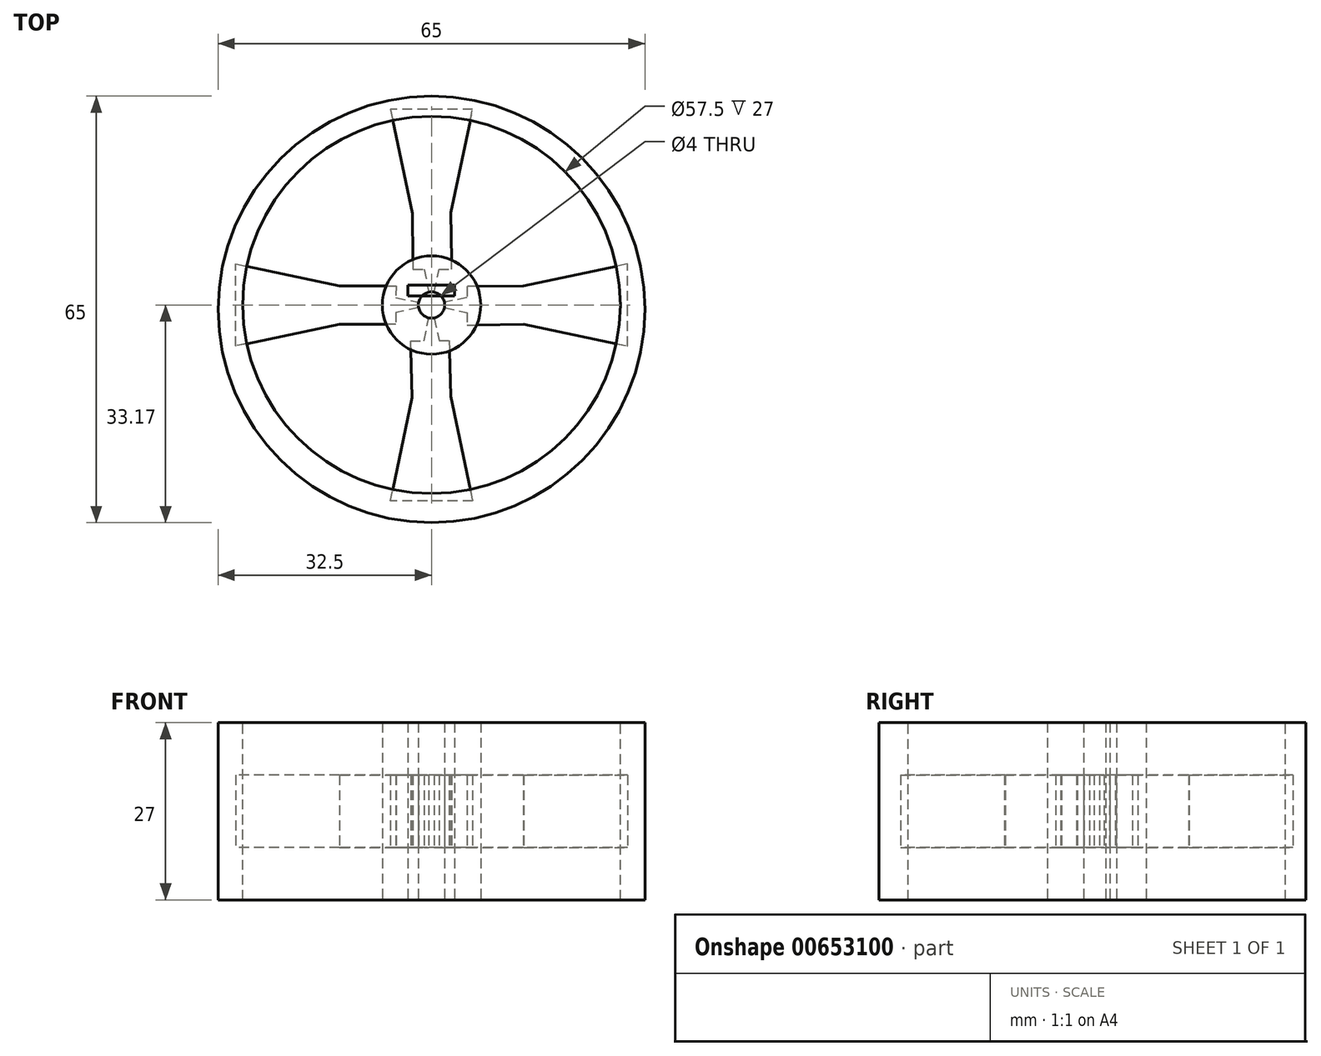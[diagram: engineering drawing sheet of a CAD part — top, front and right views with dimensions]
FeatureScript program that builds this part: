
annotation { "Feature Type Name" : "Feature", "Feature Type Description" : "" }
export const myFeature = defineFeature(function(context is Context, id is Id, definition is map)
    precondition{}
    {
        {
            var Q0;
            Q0=qCreatedBy(makeId("Top.planeOp"),FACE);
            var sketch = newSketch(context, id + "F0", { "sketchPlane" : qUnion([Q0])});
            skCircle(sketch, "E0", {"center": v(0, -0.67) * mm, "radius": 32.5 * mm});
            skSolve(sketch);
        }
        {
            var Q0;
            Q0 = qSketchRegion(id + "F0", true);
            extrude(context, id + "F1", {"entities" : qUnion([Q0]), "endBound" : BoundingType.SYMMETRIC, "depth" : 27 * mm, "offsetDistance" : 25 * mm});
        }
        {
            var Q0;
            Q0=makeQuery(id+"F1.opExtrude","CAP_FACE",FACE,{"disambiguationData":[OSD([sQuery(id+"F0.wireOp",EDGE,"E0")])],"isStart":false});
            var sketch = newSketch(context, id + "F2", { "sketchPlane" : qUnion([Q0])});
            skPoint(sketch, "E1", {"position": v(0, 0) * mm});
            skSolve(sketch);
        }
        {
            var Q0;
            Q0=sQuery(id+"F2.wireOp",VERTEX,"E1");
            var Q1;
            Q1=makeQuery(id+"F1.opExtrude","SWEPT_BODY",BODY,{"disambiguationData":[OSD([sQuery(id+"F0.wireOp",EDGE,"E0")])]});
            hole(context, id + "F3", {"style" : HoleStyle.SIMPLE, "endStyle" : HoleEndStyle.THROUGH, "holeDiameter" : 57.5 * mm, "majorDiameter" : 5 * mm, "isTappedThrough" : true, "tappedDepth" : 12 * mm, "tapClearance" : 3, "locations" : qUnion([Q0]), "scope" : qUnion([Q1])});
        }
        {
            var Q0;
            Q0=qCreatedBy(makeId("Top.planeOp"),FACE);
            var sketch = newSketch(context, id + "F4", { "sketchPlane" : qUnion([Q0])});
            skCircle(sketch, "E2", {"center": v(0, 0) * mm, "radius": 7.5 * mm});
            skSolve(sketch);
        }
        {
            var Q0;
            Q0 = qSketchRegion(id + "F4", true);
            extrude(context, id + "F5", {"entities" : qUnion([Q0]), "endBound" : BoundingType.SYMMETRIC, "depth" : 27 * mm, "offsetDistance" : 25 * mm});
        }
        {
            var Q0;
            Q0=qCreatedBy(makeId("Top.planeOp"),FACE);
            var sketch = newSketch(context, id + "F6", { "sketchPlane" : qUnion([Q0])});
            skLineSegment(sketch, "E3", {"start": v(0, 0) * mm, "end": v(6.25, -29.85) * mm});
            skLineSegment(sketch, "E4", {"start": v(6.25, -29.85) * mm, "end": v(-6.25, -29.85) * mm});
            skLineSegment(sketch, "E5", {"start": v(-6.25, -29.85) * mm, "end": v(0, 0) * mm});
            skLineSegment(sketch, "E6", {"start": v(0, 0) * mm, "end": v(29.85, -6.25) * mm});
            skLineSegment(sketch, "E7", {"start": v(29.85, -6.25) * mm, "end": v(29.85, 6.25) * mm});
            skLineSegment(sketch, "E8", {"start": v(29.85, 6.25) * mm, "end": v(0, 0) * mm});
            skLineSegment(sketch, "E9", {"start": v(0, 0) * mm, "end": v(6.25, 29.85) * mm});
            skLineSegment(sketch, "E10", {"start": v(6.25, 29.85) * mm, "end": v(-6.25, 29.85) * mm});
            skLineSegment(sketch, "E11", {"start": v(-6.25, 29.85) * mm, "end": v(0, 0) * mm});
            skLineSegment(sketch, "E12", {"start": v(0, 0) * mm, "end": v(-29.85, -6.25) * mm});
            skLineSegment(sketch, "E13", {"start": v(-29.85, -6.25) * mm, "end": v(-29.85, 6.25) * mm});
            skLineSegment(sketch, "E14", {"start": v(-29.85, 6.25) * mm, "end": v(0, 0) * mm});
            skLineSegment(sketch, "E15", {"start": v(-5.48, -2.94) * mm, "end": v(-14.02, -2.94) * mm});
            skLineSegment(sketch, "E16", {"start": v(-14.02, -2.94) * mm, "end": v(-14.02, 2.94) * mm});
            skLineSegment(sketch, "E17", {"start": v(-14.02, 2.94) * mm, "end": v(-5.4, 2.94) * mm});
            skLineSegment(sketch, "E18", {"start": v(-5.4, 2.94) * mm, "end": v(-5.48, -2.94) * mm});
            skLineSegment(sketch, "E19", {"start": v(-2.82, 5.44) * mm, "end": v(3.05, 5.44) * mm});
            skLineSegment(sketch, "E20", {"start": v(3.05, 5.44) * mm, "end": v(2.94, 14.06) * mm});
            skLineSegment(sketch, "E21", {"start": v(2.94, 14.06) * mm, "end": v(-2.93, 13.98) * mm});
            skLineSegment(sketch, "E22", {"start": v(-2.93, 13.98) * mm, "end": v(-2.82, 5.44) * mm});
            skLineSegment(sketch, "E23", {"start": v(5.44, 2.82) * mm, "end": v(5.44, -3.05) * mm});
            skLineSegment(sketch, "E24", {"start": v(5.44, -3.05) * mm, "end": v(14.06, -2.94) * mm});
            skLineSegment(sketch, "E25", {"start": v(14.06, -2.94) * mm, "end": v(13.98, 2.93) * mm});
            skLineSegment(sketch, "E26", {"start": v(13.98, 2.93) * mm, "end": v(5.44, 2.82) * mm});
            skLineSegment(sketch, "E27", {"start": v(-3.17, -5.47) * mm, "end": v(2.7, -5.4) * mm});
            skLineSegment(sketch, "E28", {"start": v(2.7, -5.4) * mm, "end": v(2.92, -13.94) * mm});
            skLineSegment(sketch, "E29", {"start": v(2.92, -13.94) * mm, "end": v(-2.95, -14.1) * mm});
            skLineSegment(sketch, "E30", {"start": v(-2.95, -14.1) * mm, "end": v(-3.17, -5.47) * mm});
            skSolve(sketch);
        }
        {
            var Q0;
            Q0 = qSketchRegion(id + "F6", true);
            extrude(context, id + "F7", {"entities" : qUnion([Q0]), "endBound" : BoundingType.SYMMETRIC, "depth" : 11 * mm, "offsetDistance" : 25 * mm});
        }
        {
            var Q0;
            Q0=makeQuery(id+"F5.opExtrude","CAP_FACE",FACE,{"disambiguationData":[OSD([sQuery(id+"F4.wireOp",EDGE,"E2")])],"isStart":true});
            var sketch = newSketch(context, id + "F8", { "sketchPlane" : qUnion([Q0])});
            skPoint(sketch, "E31", {"position": v(0, 0) * mm});
            skSolve(sketch);
        }
        {
            var Q0;
            Q0=sQuery(id+"F8.wireOp",VERTEX,"E31");
            var Q1;
            Q1=makeQuery(id+"F5.opExtrude","SWEPT_BODY",BODY,{"disambiguationData":[OSD([sQuery(id+"F4.wireOp",EDGE,"E2")])]});
            var Q2;
            Q2=makeQuery(id+"F7.opExtrude","SWEPT_BODY",BODY,{"disambiguationData":[OSD([sQuery(id+"F6.wireOp",EDGE,"E3"),sQuery(id+"F6.wireOp",EDGE,"E4"),sQuery(id+"F6.wireOp",EDGE,"E5")])]});
            var Q3;
            Q3=makeQuery(id+"F7.opExtrude","SWEPT_BODY",BODY,{"disambiguationData":[OSD([sQuery(id+"F6.wireOp",EDGE,"E6"),sQuery(id+"F6.wireOp",EDGE,"E7"),sQuery(id+"F6.wireOp",EDGE,"E8")])]});
            var Q4;
            Q4=makeQuery(id+"F7.opExtrude","SWEPT_BODY",BODY,{"disambiguationData":[OSD([sQuery(id+"F6.wireOp",EDGE,"E9"),sQuery(id+"F6.wireOp",EDGE,"E10"),sQuery(id+"F6.wireOp",EDGE,"E11")])]});
            var Q5;
            Q5=makeQuery(id+"F7.opExtrude","SWEPT_BODY",BODY,{"disambiguationData":[OSD([sQuery(id+"F6.wireOp",EDGE,"E12"),sQuery(id+"F6.wireOp",EDGE,"E13"),sQuery(id+"F6.wireOp",EDGE,"E14")])]});
            hole(context, id + "F9", {"style" : HoleStyle.SIMPLE, "endStyle" : HoleEndStyle.THROUGH, "holeDiameter" : 4 * mm, "majorDiameter" : 5 * mm, "isTappedThrough" : true, "tappedDepth" : 12 * mm, "tapClearance" : 3, "locations" : qUnion([Q0]), "scope" : qUnion([Q1, Q2, Q3, Q4, Q5])});
        }
        {
            var Q0;
            Q0=qCreatedBy(makeId("Top.planeOp"),FACE);
            var sketch = newSketch(context, id + "F10", { "sketchPlane" : qUnion([Q0])});
            skLineSegment(sketch, "E32.bottom", {"start": v(-3.58, 3.03) * mm, "end": v(3.48, 3.03) * mm});
            skLineSegment(sketch, "E32.top", {"start": v(-3.58, 1.35) * mm, "end": v(3.48, 1.35) * mm});
            skLineSegment(sketch, "E32.left", {"start": v(-3.58, 3.03) * mm, "end": v(-3.58, 1.35) * mm});
            skLineSegment(sketch, "E32.right", {"start": v(3.48, 3.03) * mm, "end": v(3.48, 1.35) * mm});
            skSolve(sketch);
        }
        {
            var Q0;
            Q0 = qSketchRegion(id + "F10", true);
            extrude(context, id + "F11", {"entities" : qUnion([Q0]), "endBound" : BoundingType.SYMMETRIC, "depth" : 27 * mm, "offsetDistance" : 25 * mm});
        }
    });
